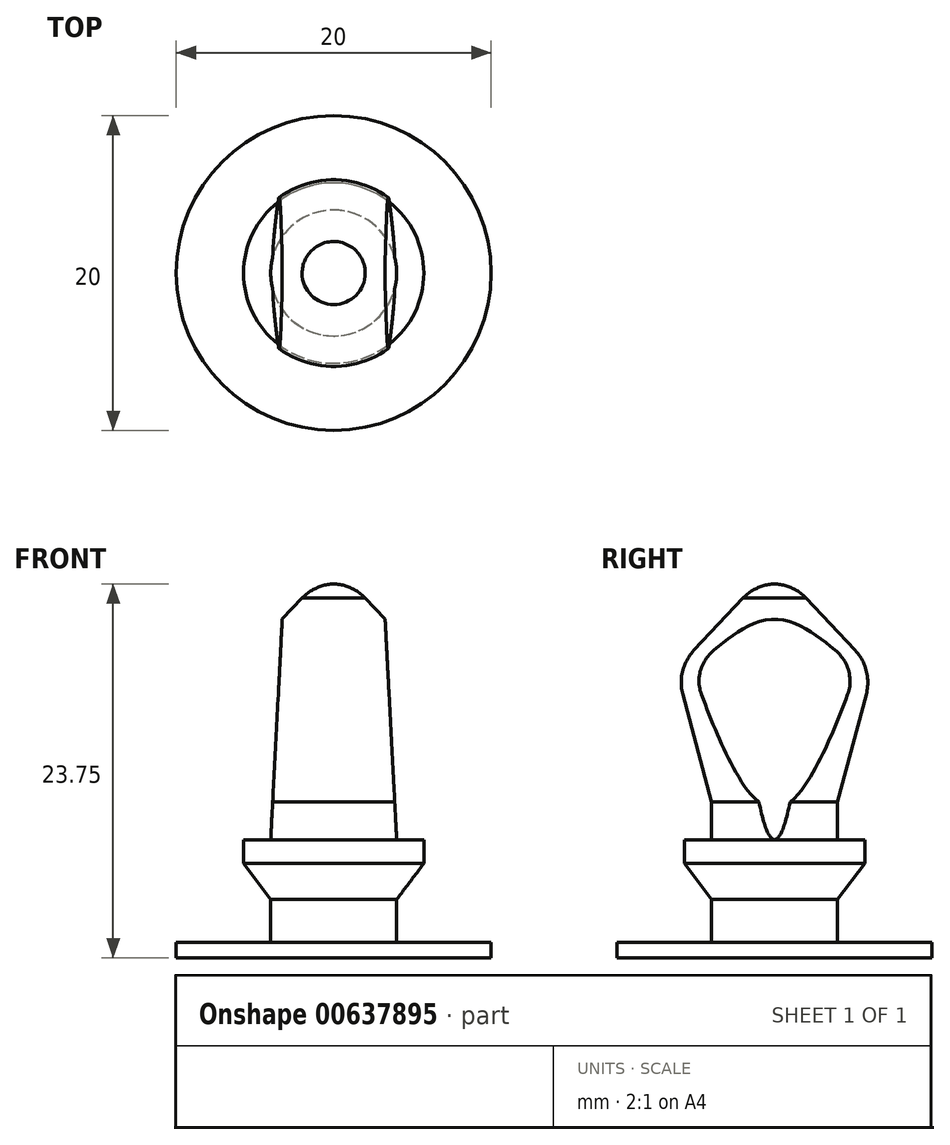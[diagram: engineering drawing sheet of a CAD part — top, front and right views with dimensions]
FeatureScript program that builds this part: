
annotation { "Feature Type Name" : "Feature", "Feature Type Description" : "" }
export const myFeature = defineFeature(function(context is Context, id is Id, definition is map)
    precondition{}
    {
        {
            var Q0;
            Q0=qCreatedBy(makeId("Front.planeOp"),FACE);
            var sketch = newSketch(context, id + "F0", { "sketchPlane" : qUnion([Q0])});
            skLineSegment(sketch, "E0", {"start": v(-4, 3.9) * mm, "end": v(-5.82, 10.72) * mm});
            skLineSegment(sketch, "E1", {"start": v(-5.11, 13.55) * mm, "end": v(-2, 16.86) * mm});
            skPoint(sketch, "E2.visualSharp", {"position": v(0, 19) * mm});
            skPoint(sketch, "E3.visualSharp", {"position": v(-6.25, 12.33) * mm});
            skArc(sketch, "E3.filletArc", {"start": v(-5.11, 13.55) * mm, "mid": v(-5.83, 12.22) * mm, "end": v(-5.82, 10.72) * mm});
            skArc(sketch, "E4", {"start": v(0, 17.75) * mm, "mid": v(-1.09, 17.5) * mm, "end": v(-2, 16.86) * mm});
            skLineSegment(sketch, "E5", {"start": v(0, 17.75) * mm, "end": v(0, 0) * mm});
            skLineSegment(sketch, "E6", {"start": v(-4, -5) * mm, "end": v(0, -5) * mm});
            skLineSegment(sketch, "E7", {"start": v(0, -5) * mm, "end": v(0, 0) * mm});
            skLineSegment(sketch, "E8", {"start": v(-5.73, 0) * mm, "end": v(-5.73, 1.5) * mm});
            skLineSegment(sketch, "E9", {"start": v(-5.73, 1.5) * mm, "end": v(-4, 1.5) * mm});
            skLineSegment(sketch, "E10", {"start": v(-4, 1.5) * mm, "end": v(-4, 3.9) * mm});
            skLineSegment(sketch, "E11", {"start": v(-5.73, 0) * mm, "end": v(-4, -2.3) * mm});
            skLineSegment(sketch, "E12", {"start": v(-4, -2.3) * mm, "end": v(-4, -5) * mm});
            skSolve(sketch);
        }
        {
            var Q0;
            Q0=makeQuery(id+"F0.imprint","IMPRINT",FACE,{"disambiguationData":[TD([[makeQuery(id+"F0.imprint","IMPRINT",EDGE,{"derivedFrom":sQuery(id+"F0.wireOp",EDGE,"E0")}),-1.0]])]});
            var Q1;
            Q1=sQuery(id+"F0.wireOp",EDGE,"E5");
            revolve(context, id + "F1", {"entities" : qUnion([Q0]), "axis" : qUnion([Q1]), "revolveType" : RevolveType.FULL});
        }
        {
            var Q0;
            Q0=makeQuery(id+"F1.opRevolve","SWEPT_FACE",FACE,{"disambiguationData":[OSD([sQuery(id+"F0.wireOp",EDGE,"E6")])]});
            var sketch = newSketch(context, id + "F2", { "sketchPlane" : qUnion([Q0])});
            skCircle(sketch, "E13", {"center": v(0, 0) * mm, "radius": 10 * mm});
            skSolve(sketch);
        }
        {
            var Q0;
            Q0 = qSketchRegion(id + "F2", true);
            extrude(context, id + "F3", {"entities" : qUnion([Q0]), "operationType" : NewBodyOperationType.ADD, "depth" : 1 * mm, "offsetDistance" : 25 * mm});
        }
        {
            var Q0;
            Q0=makeQuery(id+"F1.opRevolve","SWEPT_FACE",FACE,{"disambiguationData":[OSD([sQuery(id+"F0.wireOp",EDGE,"E9")])]});
            var sketch = newSketch(context, id + "F4", { "sketchPlane" : qUnion([Q0])});
            skLineSegment(sketch, "E14", {"start": v(-4, 0) * mm, "end": v(-4, 4.1) * mm});
            skLineSegment(sketch, "E15", {"start": v(-4, 4.1) * mm, "end": v(-4, -4.1) * mm});
            skLineSegment(sketch, "E16", {"start": v(0, 0.4) * mm, "end": v(0, 8.32) * mm, "construction": true});
            skLineSegment(sketch, "E17.MirrorCS", {"start": v(4, 4.1) * mm, "end": v(4, -4.1) * mm});
            skSolve(sketch);
        }
        {
            var Q0;
            {var subQ0=sQuery(id+"F4.wireOp",EDGE,"E15");var subQ1=sQuery(id+"F0.wireOp",EDGE,"E9");var subQ2=makeQuery(id+"F1.opRevolve","SWEPT_EDGE",EDGE,{"disambiguationData":[OSD([sQuery(id+"F0.wireOp",EDGE,"E8"),subQ1])]});var subQ3=makeQuery(id+"F4.imprint","INTERSECT",VERTEX,{"disambiguationData":[OD(0.0)],"derivedFrom":[subQ2,subQ0]});Q0=makeQuery(id+"F4.imprint","IMPRINT",FACE,{"disambiguationData":[TD([[makeQuery(id+"F4.imprint","IMPRINT",EDGE,{"disambiguationData":[TD([[subQ3,-1.0]])],"derivedFrom":subQ0}),-1.0]])]});}
            var Q1;
            {var subQ0=sQuery(id+"F4.wireOp",EDGE,"E17.MirrorCS");var subQ1=sQuery(id+"F0.wireOp",EDGE,"E9");var subQ2=makeQuery(id+"F1.opRevolve","SWEPT_EDGE",EDGE,{"disambiguationData":[OSD([sQuery(id+"F0.wireOp",EDGE,"E8"),subQ1])]});var subQ3=makeQuery(id+"F4.imprint","INTERSECT",VERTEX,{"disambiguationData":[OD(0.0)],"derivedFrom":[subQ2,subQ0]});Q1=makeQuery(id+"F4.imprint","IMPRINT",FACE,{"disambiguationData":[TD([[makeQuery(id+"F4.imprint","IMPRINT",EDGE,{"disambiguationData":[TD([[subQ3,-1.0]])],"derivedFrom":subQ0}),1.0]])]});}
            extrude(context, id + "F5", {"entities" : qUnion([Q0, Q1]), "operationType" : NewBodyOperationType.REMOVE, "depth" : 25 * mm, "offsetDistance" : 25 * mm, "hasDraft" : true, "draftAngle" : 3 * degree});
        }
    });
